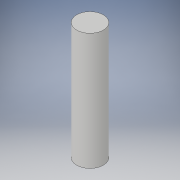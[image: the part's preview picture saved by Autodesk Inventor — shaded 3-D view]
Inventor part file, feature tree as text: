
AUTODESK INVENTOR PART (.ipt)
format: ipt  version: 2019 (Build 230136000, 136)  size: 88,576 bytes
history: native  units: mm
features: extrude x1, sketch x1
ambient origin geometry x8: Origin, YZ Plane, XZ Plane, XY Plane, X Axis, Y Axis, Z Axis, Center Point
bodies: Solid1 (feature_tree)
feature tree (2):
  extrude  "Extrusion1"  Depth=22.0mm TaperAngle=0.0deg
  sketch  "Sketch1"  dims[d0=5.0mm d1=22.0mm d2=0.0mm]
